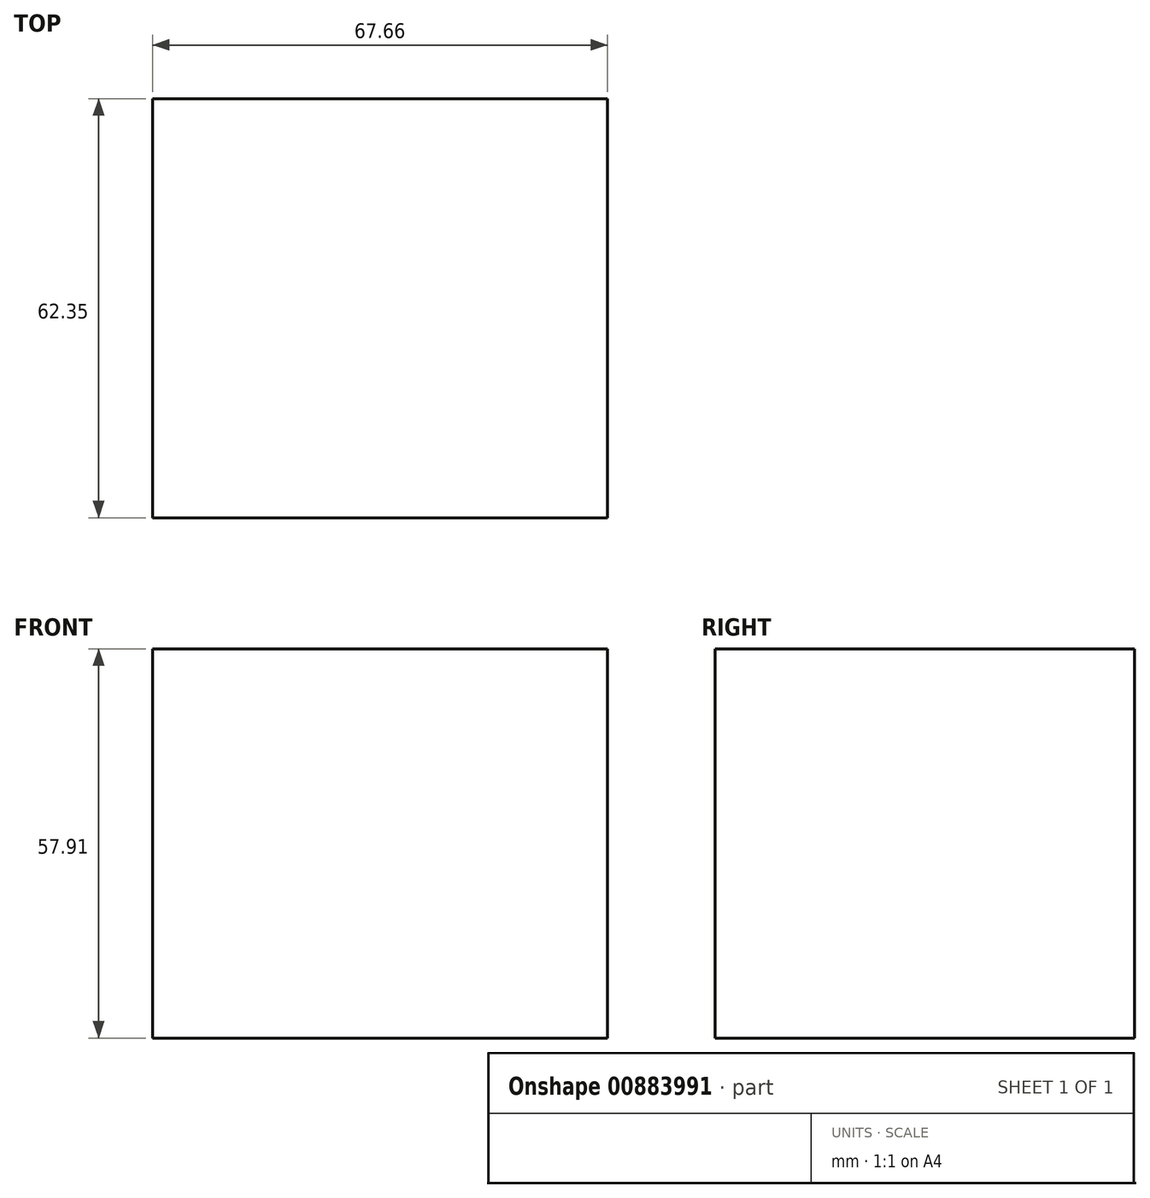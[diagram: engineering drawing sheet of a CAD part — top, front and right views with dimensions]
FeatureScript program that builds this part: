
annotation { "Feature Type Name" : "Feature", "Feature Type Description" : "" }
export const myFeature = defineFeature(function(context is Context, id is Id, definition is map)
    precondition{}
    {
        {
            var Q0;
            Q0=qCreatedBy(makeId("Top.planeOp"),FACE);
            var sketch = newSketch(context, id + "F0", { "sketchPlane" : qUnion([Q0])});
            skLineSegment(sketch, "E0.bottom", {"start": v(0, 0) * mm, "end": v(67.66, 0) * mm});
            skLineSegment(sketch, "E0.top", {"start": v(0, -62.35) * mm, "end": v(67.66, -62.35) * mm});
            skLineSegment(sketch, "E0.left", {"start": v(0, 0) * mm, "end": v(0, -62.35) * mm});
            skLineSegment(sketch, "E0.right", {"start": v(67.66, 0) * mm, "end": v(67.66, -62.35) * mm});
            skSolve(sketch);
        }
        {
            var Q0;
            Q0=makeQuery(id+"F0.imprint","IMPRINT",FACE,{"disambiguationData":[TD([[makeQuery(id+"F0.imprint","IMPRINT",EDGE,{"derivedFrom":sQuery(id+"F0.wireOp",EDGE,"E0.bottom")}),-1.0]])]});
            extrude(context, id + "F1", {"entities" : qUnion([Q0]), "depth" : 57.9 * mm, "offsetDistance" : 25.4 * mm});
        }
    });
